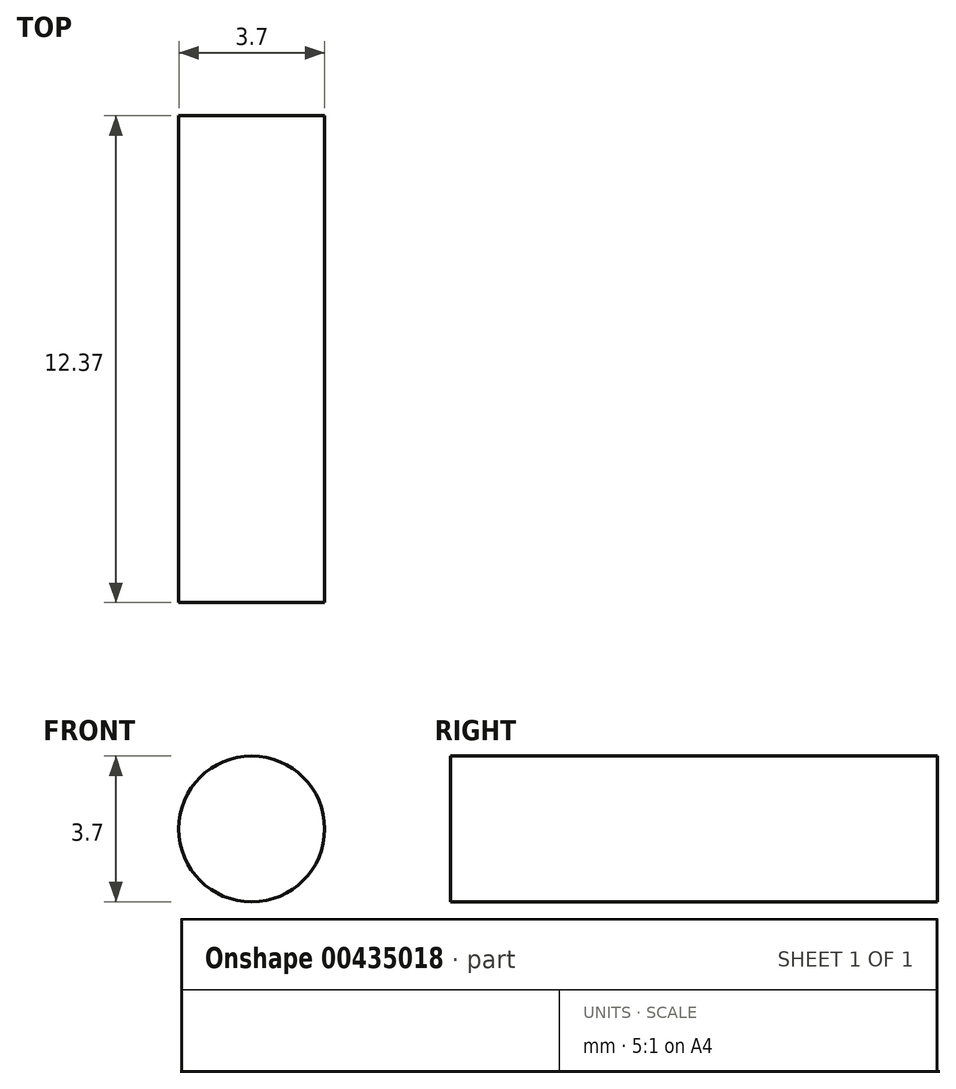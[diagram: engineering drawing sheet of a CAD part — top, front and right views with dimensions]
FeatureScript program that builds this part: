
annotation { "Feature Type Name" : "Feature", "Feature Type Description" : "" }
export const myFeature = defineFeature(function(context is Context, id is Id, definition is map)
    precondition{}
    {
        {
            var Q0;
            Q0=qCreatedBy(makeId("Front.planeOp"),FACE);
            var sketch = newSketch(context, id + "F0", { "sketchPlane" : qUnion([Q0])});
            skCircle(sketch, "E0", {"center": v(0, 0) * mm, "radius": 1.85 * mm});
            skSolve(sketch);
        }
        {
            var Q0;
            Q0 = qSketchRegion(id + "F0", true);
            extrude(context, id + "F1", {"entities" : qUnion([Q0]), "depth" : 12.37 * mm});
        }
    });
